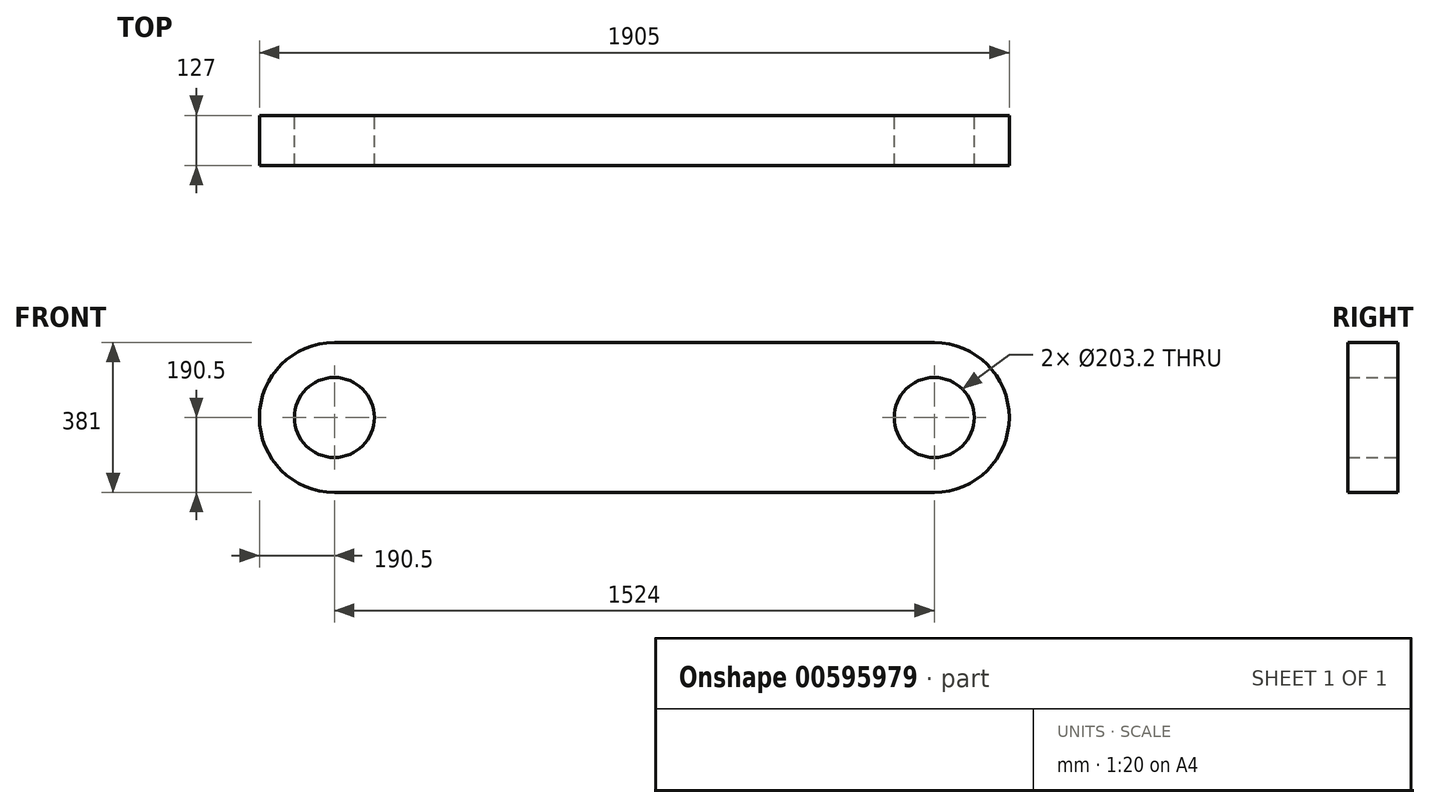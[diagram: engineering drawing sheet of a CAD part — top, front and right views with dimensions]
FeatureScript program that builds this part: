
annotation { "Feature Type Name" : "Feature", "Feature Type Description" : "" }
export const myFeature = defineFeature(function(context is Context, id is Id, definition is map)
    precondition{}
    {
        {
            var Q0;
            Q0=qCreatedBy(makeId("Front.planeOp"),FACE);
            var sketch = newSketch(context, id + "F0", { "sketchPlane" : qUnion([Q0])});
            skArc(sketch, "E0", {"start": v(0, 190.5) * mm, "mid": v(-190.5, 0) * mm, "end": v(0, -190.5) * mm});
            skArc(sketch, "E1", {"start": v(1524, -190.5) * mm, "mid": v(1714.5, 0) * mm, "end": v(1524, 190.5) * mm});
            skLineSegment(sketch, "E2", {"start": v(0, 190.5) * mm, "end": v(1524, 190.5) * mm});
            skLineSegment(sketch, "E3", {"start": v(0, -190.5) * mm, "end": v(1524, -190.5) * mm});
            skCircle(sketch, "E4", {"center": v(0, 0) * mm, "radius": 101.6 * mm});
            skCircle(sketch, "E5", {"center": v(1524, 0) * mm, "radius": 101.6 * mm});
            skSolve(sketch);
        }
        {
            var Q0;
            Q0=makeQuery(id+"F0.imprint","IMPRINT",FACE,{"disambiguationData":[TD([[makeQuery(id+"F0.imprint","IMPRINT",EDGE,{"derivedFrom":sQuery(id+"F0.wireOp",EDGE,"E0")}),1.0]])]});
            extrude(context, id + "F1", {"entities" : qUnion([Q0]), "depth" : 127 * mm, "offsetDistance" : 25.4 * mm});
        }
    });
